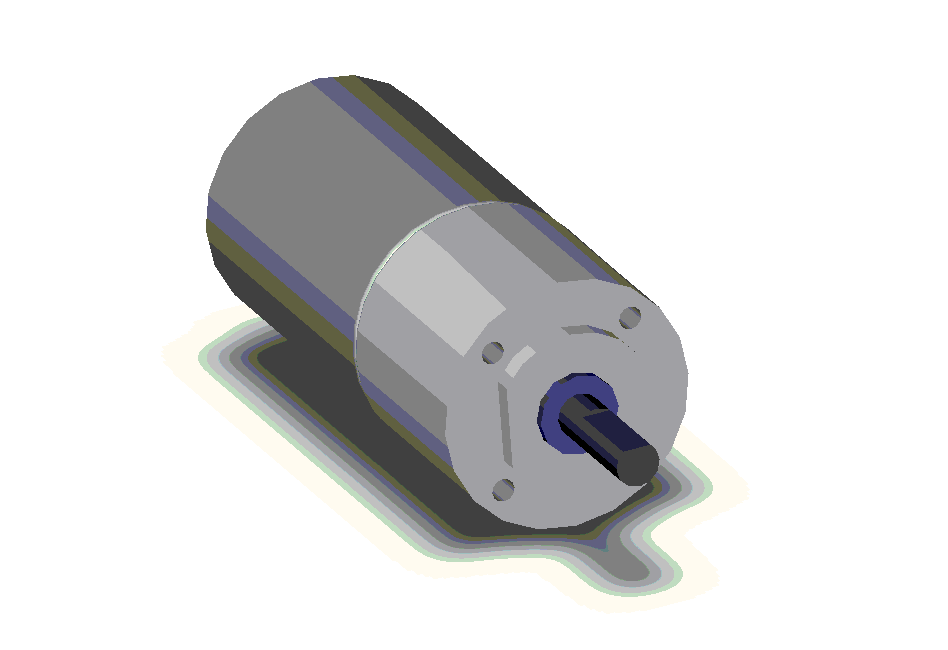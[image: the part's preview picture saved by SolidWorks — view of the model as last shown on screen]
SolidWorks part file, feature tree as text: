
SOLIDWORKS PART (.sldprt)
format: sldprt  version: not decoded by parser v0  size: 334,336 bytes
history: native  units: mm
features: sketch x9, extrude x7, fillet x5, cut_extrude x2, pattern_circular x1 (+8 scaffold rows collapsed)
feature tree (32):
  scaffold x8  (default folders/planes/origin — collapsed)
  sketch  "Sketch1"  dims[D1=21.9mm]
  extrude  "Base-Extrude"  Depth=18mm
  sketch  "Sketch3"  dims[D1=13.88mm D2=5.94mm D3=11.88mm]
  extrude  "Boss-Extrude1"  Depth=1.75mm
  sketch  "Sketch4"  dims[D1=7.01mm]
  extrude  "Boss-Extrude2"  Depth=0.8mm
  sketch  "Sketch5"  dims[D1=3.89mm]
  extrude  "Boss-Extrude3"  Depth=11.5mm
  fillet  "Fillet1"  Radius=0.5mm
  sketch  "Sketch6"  dims[D1=21.66mm]
  extrude  "Boss-Extrude4"  Depth=29.5mm
  fillet  "Fillet2"  Radius=0.5mm
  sketch  "Sketch7"  dims[D1=7.37mm]
  extrude  "Boss-Extrude5"  Depth=2.47mm
  sketch  "Sketch8"  dims[c1.D1=~8.417389mm c2.D1=45.0deg c2.D2=1.93mm c2.D3=0.965mm c2.D4=0.11mm c2.D5=8.5mm c3.D1=8.5mm c3.D3=0.965mm c3.D5=~5.250268mm c3.D6=0.11mm c3.D7=8.5mm c3.D8=1.93mm]
  extrude  "Boss-Extrude6"  Depth=3.18mm
  fillet  "Fillet3"  Radius=0.9mm
  fillet  "Fillet4"  Radius=0.9mm
  fillet  "Fillet5"  Radius=0.9mm
  sketch  "Sketch9"  dims[D1=1.5mm D2=2.0mm D3=4.0mm D4=2.0mm]
  cut_extrude  "Cut-Extrude1"  Depth=8mm
  sketch  "Sketch10"  dims[c1.D2=2.0mm c1.D3=17.5mm c1.D1=~14.25192mm c2.D1=45.0deg c3.D1=8.75mm c3.D3=~6.187184mm]
  cut_extrude  "Cut-Extrude2"  Depth=4mm
  pattern_circular  "CirPattern1"  Count=4 Angle=90deg
decode coverage: 24 of 24 modeling features carry decoded parameters
note: ~ marks probable driven/reference dimensions
note: suppression state not decoded; provenance and decode notes live in map.json
